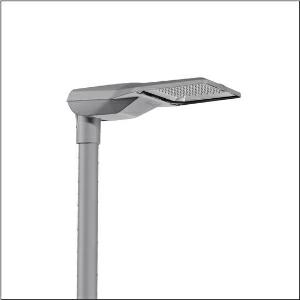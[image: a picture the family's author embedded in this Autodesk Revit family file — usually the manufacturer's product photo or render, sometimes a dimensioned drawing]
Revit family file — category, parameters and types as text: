
# Revit family: streetlight_sl_21_midi___st1_0ab_5xe7m33a08nb_abda
name_source: partatom
category: Lighting Fixtures
units: mm (PartAtom-declared; Revit-internal decimal feet)

## family parameters
Cut with Voids When Loaded = No
Host = Face
Light Source = No
Part Type = Normal
Room Calculation Point = No
Round Connector Dimension = Use Diameter
Shared = No

## types (1)
- --- (1 x LED, 19980 lm, 151.2 W, 3000K)
    Apparent Load = 151 VA
    CIE Flux Codes = 40 74 97 100 100
    Color Rendering = 70
    Color Temperature = 3000K
    Default Elevation = 1800 mm
    Description = Streetlight SL 21 midi, mast luminaire, primary light control with lens, of PMMA, primary optical cover: cover, of toughened safety glass, transparent, light distribution: ST1.0aB, light emission: direct distribution, primary light characteristic: asymmetric, installation type: post-top, side-entry, LED, 3G 1.5mm², High Power LED, rated luminous flux: 19.980lm, luminous efficacy: 132lm/W, light colour: 730, colour temperature: 3000K, control: flexible luminous flux parameterisation, time-dependent luminous flux control, constant luminous flux control, overheat protection, mains connection: 220..240V, AC, 50/60Hz, connection cable pre-assembled, cable length: 12,5m, wiring characteristics: H07RN-F, start of lifetime: 151W, end of service life: 157W, reduction: 70W, luminaire housing, of diecast aluminium, powder-coated, Siteco® metallic grey (DB 702S), corrosivity category C5 mid according to DIN EN ISO 12944, please order mast flange separately, inclination adjustable: 0°, 5°, 10°, 15°, sealing non-destructively replaceable, multi-level sealing system, length: 644mm, width: 335mm, height: 110mm, mast flange for spigot size: 42mm (side-entry): 5XC10008XM4, 60/48mm (side-entry/post-top): 5XC10108XM2, 76/60mm (side-entry/post-top): 5XC10108XM1, protection rating (complete): IP66, insulation class (complete): insulation class II (safety insulation), certification: CE, ENEC, ENEC+, VDE, impact resistance: IK09, permissible operating ambient temperature for outdoor applications: -40..+50°C, standard-compliant lighting for roads and squares, packaging unit: 1 piece

Light Distribution: ST1.0aB
    Height = 111 mm
    Lamp = 1 x LED
    Lamp Light Flux = 19980 lm
    Lamp Power = 151.2 W
    Lamp count = 1
    Length = 644 mm
    Luminous efficacy = 132 lm/W
    Manufacturer = Siteco
    ModVariant = No
    Model = 5XE7M33A08NB
    Number of Poles = 1
    OnlyDefault = Yes
    Power Factor = 1
    Product Name = Streetlight SL 21 midi | ST1.0aB
    Product group = mast luminaire | pylon top
    ProductGroupID = 6100
    Protection Class = Protection class II
    Protection Degree = IP 66
    RLX_Detail_Level = 1
    RLX_Emergency_Light_Flux = 0 lm
    RLX_Emergency_Type = 0
    RLX_Emergency_Type_DB = No
    RlxData = <blob elided: 90593 chars, md5=d79ddf85>
    Socket = socket
    Standby Power = 0 W
    System Light Flux = 19980 lm
    System Power = 151 W
    Type Comments = factory setting: luminous flux: 100 % | Output Level: 100 % | 802 mA
    Type Image = l_1004298.jpg
    URL = http://relux.com
    VarID = @adj_118199
    Voltage = 0 V
    Weight = 0.00 kg
    Width = 336 mm

## geometry (parser evidence)
native form markers: Blend x4, Sweep x9
no freeform markers — native parametric forms only
